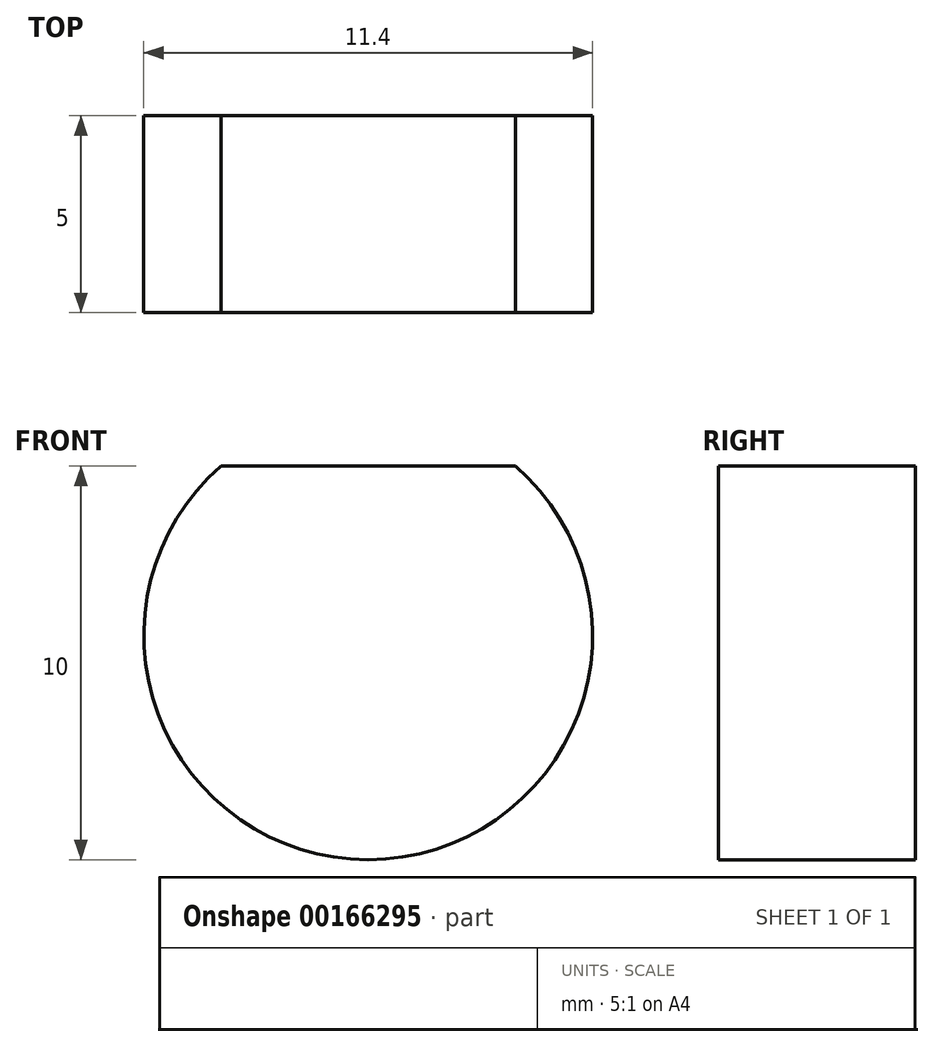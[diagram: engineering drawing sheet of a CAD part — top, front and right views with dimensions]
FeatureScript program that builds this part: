
annotation { "Feature Type Name" : "Feature", "Feature Type Description" : "" }
export const myFeature = defineFeature(function(context is Context, id is Id, definition is map)
    precondition{}
    {
        {
            assignVariable(context, id + "F0", {"name" : "Main_Length", "anyValue" : 5});
        }
        {
            var Q0;
            Q0=qCreatedBy(makeId("Front.planeOp"),FACE);
            var sketch = newSketch(context, id + "F1", { "sketchPlane" : qUnion([Q0])});
            skArc(sketch, "E0", {"start": v(-3.74, 4.3) * mm, "mid": v(0, -5.7) * mm, "end": v(3.74, 4.3) * mm});
            skLineSegment(sketch, "E1", {"start": v(-3.74, 4.3) * mm, "end": v(3.74, 4.3) * mm});
            skSolve(sketch);
        }
        {
            var Q0;
            Q0=makeQuery(id+"F1.imprint","IMPRINT",FACE,{"disambiguationData":[TD([[makeQuery(id+"F1.imprint","IMPRINT",EDGE,{"derivedFrom":sQuery(id+"F1.wireOp",EDGE,"E0")}),1.0]])]});
            extrude(context, id + "F2", {"entities" : qUnion([Q0]), "depth" : (getVariable(context, 'Main_Length')) * mm});
        }
    });
